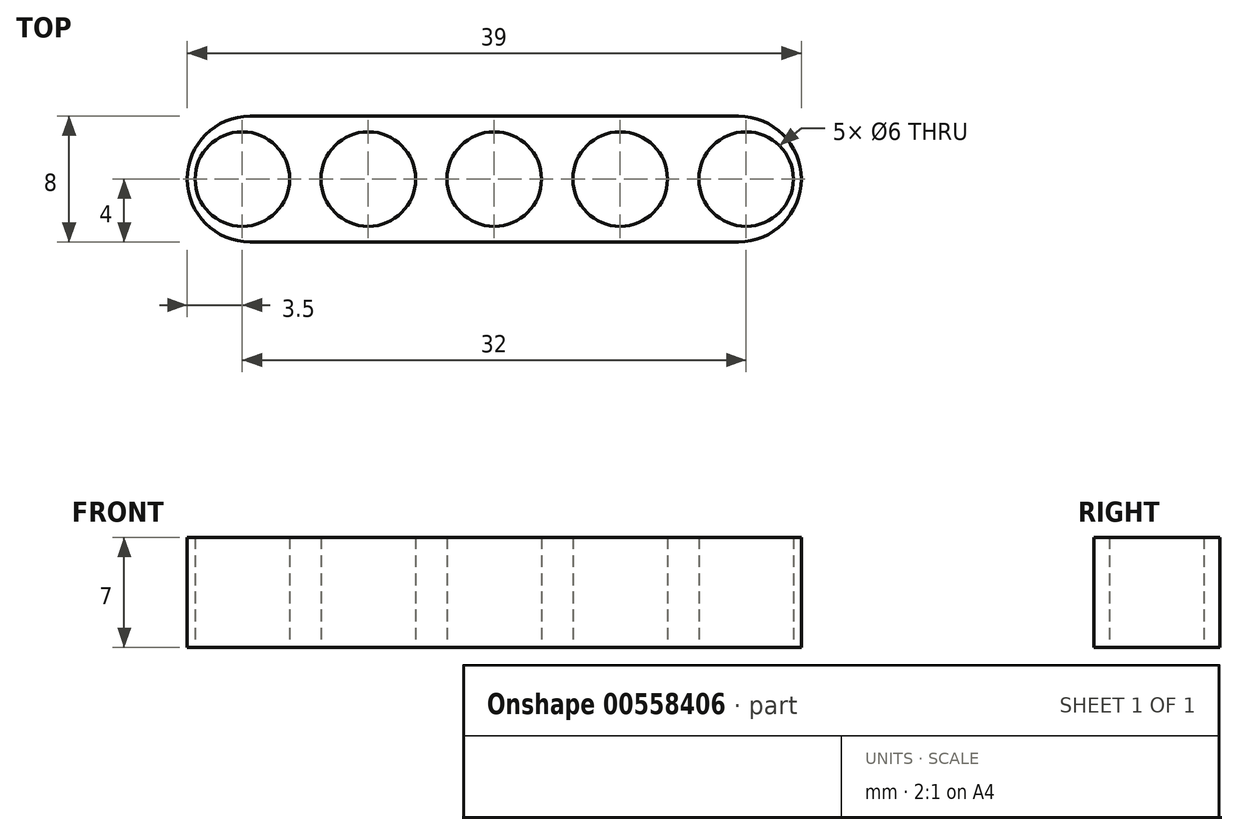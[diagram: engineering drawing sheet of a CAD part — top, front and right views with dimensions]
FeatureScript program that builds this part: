
annotation { "Feature Type Name" : "Feature", "Feature Type Description" : "" }
export const myFeature = defineFeature(function(context is Context, id is Id, definition is map)
    precondition{}
    {
        {
            var Q0;
            Q0=qCreatedBy(makeId("Top.planeOp"),FACE);
            var sketch = newSketch(context, id + "F0", { "sketchPlane" : qUnion([Q0])});
            skLineSegment(sketch, "E0.bottom", {"start": v(19.5, 4) * mm, "end": v(-19.5, 4) * mm});
            skLineSegment(sketch, "E0.top", {"start": v(19.5, -4) * mm, "end": v(-19.5, -4) * mm});
            skLineSegment(sketch, "E0.left", {"start": v(19.5, 4) * mm, "end": v(19.5, -4) * mm});
            skLineSegment(sketch, "E0.right", {"start": v(-19.5, 4) * mm, "end": v(-19.5, -4) * mm});
            skPoint(sketch, "E0.middle", {"position": v(0, 0) * mm});
            skCircle(sketch, "E1", {"center": v(0, 0) * mm, "radius": 3 * mm});
            skCircle(sketch, "E2.1.0.0", {"center": v(8, 0) * mm, "radius": 3 * mm});
            skCircle(sketch, "E2.2.0.0", {"center": v(16, 0) * mm, "radius": 3 * mm});
            skLineSegment(sketch, "E2.direction1", {"start": v(0, 0) * mm, "end": v(8, 0) * mm, "construction": true});
            skCircle(sketch, "E3.1.0.0", {"center": v(-8, 0) * mm, "radius": 3 * mm});
            skCircle(sketch, "E3.2.0.0", {"center": v(-16, 0) * mm, "radius": 3 * mm});
            skLineSegment(sketch, "E3.direction1", {"start": v(0, 0) * mm, "end": v(-8, 0) * mm, "construction": true});
            skSolve(sketch);
        }
        {
            var Q0;
            Q0=makeQuery(id+"F0.imprint","IMPRINT",FACE,{"disambiguationData":[TD([[makeQuery(id+"F0.imprint","IMPRINT",EDGE,{"derivedFrom":sQuery(id+"F0.wireOp",EDGE,"E0.bottom")}),1.0]])]});
            extrude(context, id + "F1", {"entities" : qUnion([Q0]), "depth" : 7 * mm, "offsetDistance" : 25.4 * mm});
        }
        {
            var Q0;
            Q0=makeQuery(id+"F1.opExtrude","SWEPT_EDGE",EDGE,{"disambiguationData":[OSD([sQuery(id+"F0.wireOp",EDGE,"E0.bottom"),sQuery(id+"F0.wireOp",EDGE,"E0.right")])]});
            var Q1;
            Q1=makeQuery(id+"F1.opExtrude","SWEPT_EDGE",EDGE,{"disambiguationData":[OSD([sQuery(id+"F0.wireOp",EDGE,"E0.top"),sQuery(id+"F0.wireOp",EDGE,"E0.right")])]});
            var Q2;
            Q2=makeQuery(id+"F1.opExtrude","SWEPT_EDGE",EDGE,{"disambiguationData":[OSD([sQuery(id+"F0.wireOp",EDGE,"E0.top"),sQuery(id+"F0.wireOp",EDGE,"E0.left")])]});
            var Q3;
            Q3=makeQuery(id+"F1.opExtrude","SWEPT_EDGE",EDGE,{"disambiguationData":[OSD([sQuery(id+"F0.wireOp",EDGE,"E0.bottom"),sQuery(id+"F0.wireOp",EDGE,"E0.left")])]});
            fillet(context, id + "F2", {"entities" : qUnion([Q0, Q1, Q2, Q3]), "radius" : 4 * mm, "tangentPropagation" : true, "allowEdgeOverflow" : false});
        }
    });
